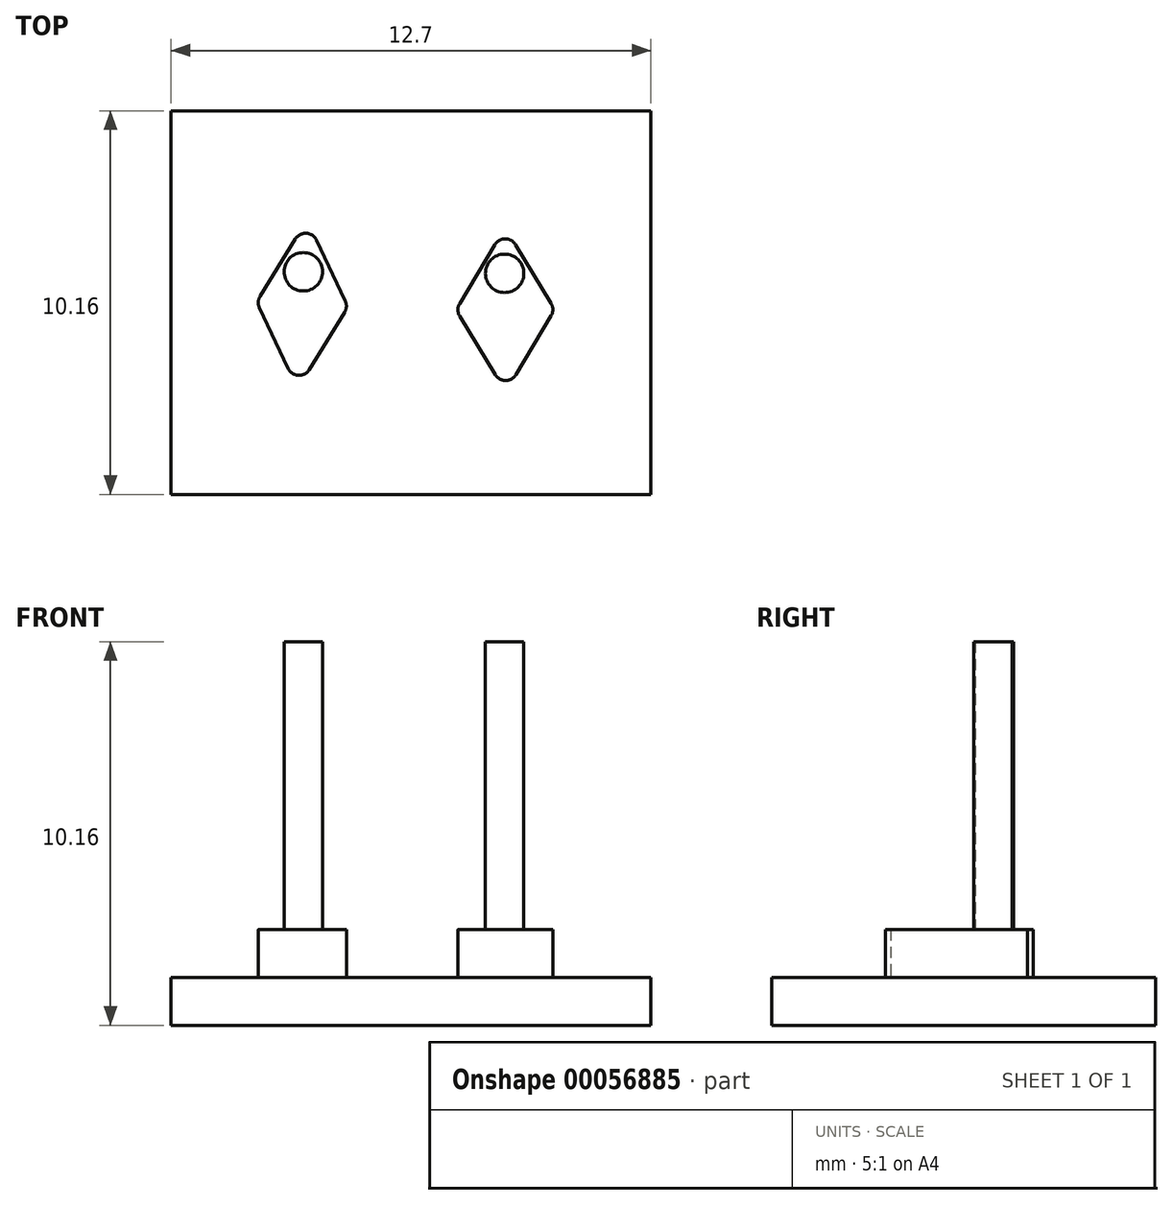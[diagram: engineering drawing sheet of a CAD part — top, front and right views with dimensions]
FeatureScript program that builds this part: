
annotation { "Feature Type Name" : "Feature", "Feature Type Description" : "" }
export const myFeature = defineFeature(function(context is Context, id is Id, definition is map)
    precondition{}
    {
        {
            var Q0;
            Q0=qCreatedBy(makeId("Top.planeOp"),FACE);
            var sketch = newSketch(context, id + "F0", { "sketchPlane" : qUnion([Q0])});
            skLineSegment(sketch, "E0", {"start": v(0, 0) * mm, "end": v(12.7, 0) * mm});
            skLineSegment(sketch, "E1", {"start": v(12.7, 0) * mm, "end": v(12.7, -10.16) * mm});
            skLineSegment(sketch, "E2", {"start": v(12.7, -10.16) * mm, "end": v(0, -10.16) * mm});
            skLineSegment(sketch, "E3", {"start": v(0, -10.16) * mm, "end": v(0, 0) * mm});
            skSolve(sketch);
        }
        {
            var Q0;
            Q0=makeQuery(id+"F0.imprint","IMPRINT",FACE,{"disambiguationData":[TD([[makeQuery(id+"F0.imprint","IMPRINT",EDGE,{"derivedFrom":sQuery(id+"F0.wireOp",EDGE,"E0")}),-1.0]])]});
            extrude(context, id + "F1", {"entities" : qUnion([Q0]), "depth" : 1.27 * mm});
        }
        {
            var Q0;
            Q0=makeQuery(id+"F1.opExtrude","CAP_FACE",FACE,{"disambiguationData":[OSD([sQuery(id+"F0.wireOp",EDGE,"E0"),sQuery(id+"F0.wireOp",EDGE,"E1"),sQuery(id+"F0.wireOp",EDGE,"E2"),sQuery(id+"F0.wireOp",EDGE,"E3")])],"isStart":false});
            var sketch = newSketch(context, id + "F2", { "sketchPlane" : qUnion([Q0])});
            skLineSegment(sketch, "E4", {"start": v(3.6, -2.9) * mm, "end": v(2.27, -5.06) * mm});
            skLineSegment(sketch, "E5", {"start": v(2.27, -5.06) * mm, "end": v(3.35, -7.36) * mm});
            skLineSegment(sketch, "E6", {"start": v(3.35, -7.36) * mm, "end": v(4.68, -5.2) * mm});
            skLineSegment(sketch, "E7", {"start": v(4.68, -5.2) * mm, "end": v(3.6, -2.9) * mm});
            skLineSegment(sketch, "E8", {"start": v(8.86, -7.45) * mm, "end": v(7.54, -5.27) * mm});
            skLineSegment(sketch, "E9", {"start": v(7.54, -5.27) * mm, "end": v(8.84, -3.1) * mm});
            skLineSegment(sketch, "E10", {"start": v(8.84, -3.1) * mm, "end": v(10.16, -5.26) * mm});
            skLineSegment(sketch, "E11", {"start": v(10.16, -5.26) * mm, "end": v(8.86, -7.45) * mm});
            skSolve(sketch);
        }
        {
            var Q0;
            Q0=makeQuery(id+"F2.imprint","IMPRINT",FACE,{"disambiguationData":[TD([[makeQuery(id+"F2.imprint","IMPRINT",EDGE,{"derivedFrom":sQuery(id+"F2.wireOp",EDGE,"E4")}),1.0]])]});
            var Q1;
            Q1=makeQuery(id+"F2.imprint","IMPRINT",FACE,{"disambiguationData":[TD([[makeQuery(id+"F2.imprint","IMPRINT",EDGE,{"derivedFrom":sQuery(id+"F2.wireOp",EDGE,"E8")}),-1.0]])]});
            extrude(context, id + "F3", {"entities" : qUnion([Q0, Q1]), "operationType" : NewBodyOperationType.ADD, "depth" : 1.27 * mm});
        }
        {
            var Q0;
            Q0=makeQuery(id+"F3.opExtrude","SWEPT_EDGE",EDGE,{"disambiguationData":[OSD([sQuery(id+"F2.wireOp",EDGE,"E5"),sQuery(id+"F2.wireOp",EDGE,"E6")])]});
            var Q1;
            Q1=makeQuery(id+"F3.opExtrude","SWEPT_EDGE",EDGE,{"disambiguationData":[OSD([sQuery(id+"F2.wireOp",EDGE,"E8"),sQuery(id+"F2.wireOp",EDGE,"E11")])]});
            fillet(context, id + "F4", {"entities" : qUnion([Q0, Q1]), "radius" : 0.32 * mm, "tangentPropagation" : true, "allowEdgeOverflow" : false});
        }
        {
            var Q0;
            Q0=makeQuery(id+"F3.opExtrude","SWEPT_EDGE",EDGE,{"disambiguationData":[OSD([sQuery(id+"F2.wireOp",EDGE,"E8"),sQuery(id+"F2.wireOp",EDGE,"E9")])]});
            var Q1;
            Q1=makeQuery(id+"F3.opExtrude","SWEPT_EDGE",EDGE,{"disambiguationData":[OSD([sQuery(id+"F2.wireOp",EDGE,"E4"),sQuery(id+"F2.wireOp",EDGE,"E5")])]});
            var Q2;
            Q2=makeQuery(id+"F3.opExtrude","SWEPT_EDGE",EDGE,{"disambiguationData":[OSD([sQuery(id+"F2.wireOp",EDGE,"E4"),sQuery(id+"F2.wireOp",EDGE,"E7")])]});
            var Q3;
            Q3=makeQuery(id+"F3.opExtrude","SWEPT_EDGE",EDGE,{"disambiguationData":[OSD([sQuery(id+"F2.wireOp",EDGE,"E9"),sQuery(id+"F2.wireOp",EDGE,"E10")])]});
            var Q4;
            Q4=makeQuery(id+"F3.opExtrude","SWEPT_EDGE",EDGE,{"disambiguationData":[OSD([sQuery(id+"F2.wireOp",EDGE,"E10"),sQuery(id+"F2.wireOp",EDGE,"E11")])]});
            var Q5;
            Q5=makeQuery(id+"F3.opExtrude","SWEPT_EDGE",EDGE,{"disambiguationData":[OSD([sQuery(id+"F2.wireOp",EDGE,"E6"),sQuery(id+"F2.wireOp",EDGE,"E7")])]});
            fillet(context, id + "F5", {"entities" : qUnion([Q0, Q1, Q2, Q3, Q4, Q5]), "radius" : 0.32 * mm, "tangentPropagation" : true, "allowEdgeOverflow" : false});
        }
        {
            var Q0;
            Q0=makeQuery(id+"F3.opExtrude","CAP_FACE",FACE,{"disambiguationData":[OSD([sQuery(id+"F2.wireOp",EDGE,"E4"),sQuery(id+"F2.wireOp",EDGE,"E5"),sQuery(id+"F2.wireOp",EDGE,"E6"),sQuery(id+"F2.wireOp",EDGE,"E7")])],"isStart":false});
            var sketch = newSketch(context, id + "F6", { "sketchPlane" : qUnion([Q0])});
            skCircle(sketch, "E12", {"center": v(3.5, -4.27) * mm, "radius": 0.5 * mm});
            skSolve(sketch);
        }
        {
            var Q0;
            Q0=makeQuery(id+"F6.imprint","IMPRINT",FACE,{"disambiguationData":[TD([[makeQuery(id+"F6.imprint","IMPRINT",EDGE,{"derivedFrom":sQuery(id+"F6.wireOp",EDGE,"E12")}),1.0]])]});
            extrude(context, id + "F7", {"entities" : qUnion([Q0]), "operationType" : NewBodyOperationType.ADD, "depth" : 7.62 * mm});
        }
        {
            var Q0;
            Q0=makeQuery(id+"F3.opExtrude","CAP_FACE",FACE,{"disambiguationData":[OSD([sQuery(id+"F2.wireOp",EDGE,"E8"),sQuery(id+"F2.wireOp",EDGE,"E9"),sQuery(id+"F2.wireOp",EDGE,"E10"),sQuery(id+"F2.wireOp",EDGE,"E11")])],"isStart":false});
            var sketch = newSketch(context, id + "F8", { "sketchPlane" : qUnion([Q0])});
            skCircle(sketch, "E13", {"center": v(8.83, -4.3) * mm, "radius": 0.5 * mm});
            skSolve(sketch);
        }
        {
            var Q0;
            Q0=makeQuery(id+"F8.imprint","IMPRINT",FACE,{"disambiguationData":[TD([[makeQuery(id+"F8.imprint","IMPRINT",EDGE,{"derivedFrom":sQuery(id+"F8.wireOp",EDGE,"E13")}),1.0]])]});
            extrude(context, id + "F9", {"entities" : qUnion([Q0]), "operationType" : NewBodyOperationType.ADD, "depth" : 7.62 * mm});
        }
    });
